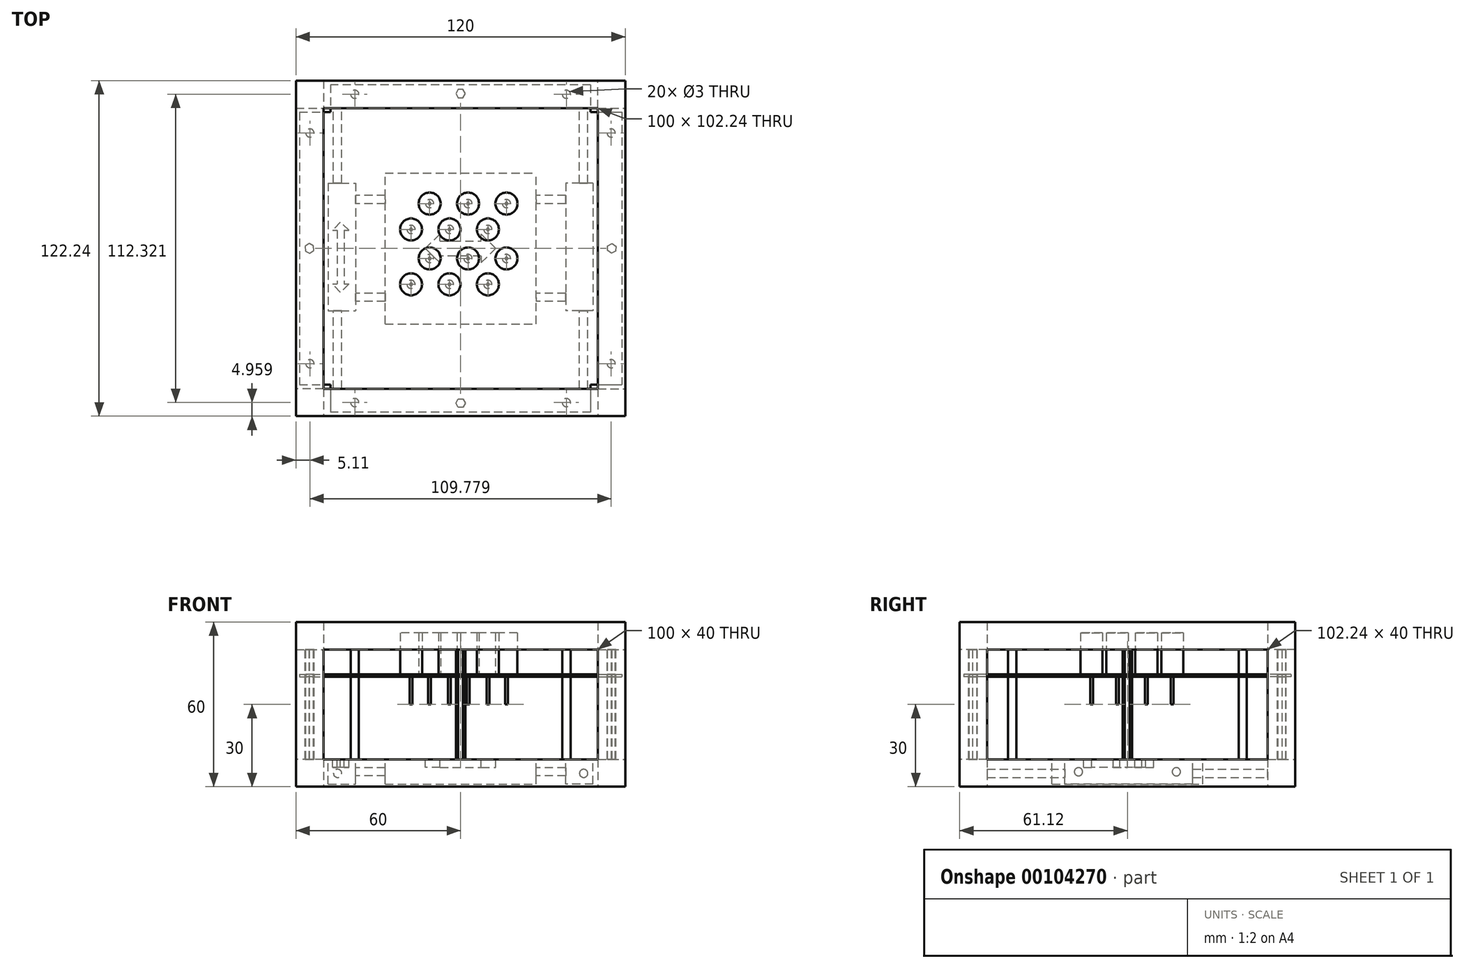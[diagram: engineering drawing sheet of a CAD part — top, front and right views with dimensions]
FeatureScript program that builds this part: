
annotation { "Feature Type Name" : "Feature", "Feature Type Description" : "" }
export const myFeature = defineFeature(function(context is Context, id is Id, definition is map)
    precondition{}
    {
        {
            var Q0;
            Q0=qCreatedBy(makeId("Top.planeOp"),FACE);
            var sketch = newSketch(context, id + "F0", { "sketchPlane" : qUnion([Q0])});
            skLineSegment(sketch, "E0.bottom", {"start": v(60, 61.12) * mm, "end": v(-60, 61.12) * mm});
            skLineSegment(sketch, "E0.top", {"start": v(60, -61.12) * mm, "end": v(-60, -61.12) * mm});
            skLineSegment(sketch, "E0.left", {"start": v(60, 61.12) * mm, "end": v(60, -61.12) * mm});
            skLineSegment(sketch, "E0.right", {"start": v(-60, 61.12) * mm, "end": v(-60, -61.12) * mm});
            skPoint(sketch, "E0.middle", {"position": v(0, 0) * mm});
            skLineSegment(sketch, "E1.bottom", {"start": v(50, 51.12) * mm, "end": v(-50, 51.12) * mm});
            skLineSegment(sketch, "E1.top", {"start": v(50, -51.12) * mm, "end": v(-50, -51.12) * mm});
            skLineSegment(sketch, "E1.left", {"start": v(50, 51.12) * mm, "end": v(50, -51.12) * mm});
            skLineSegment(sketch, "E1.right", {"start": v(-50, 51.12) * mm, "end": v(-50, -51.12) * mm});
            skSolve(sketch);
        }
        {
            var Q0;
            Q0 = qSketchRegion(id + "F0", true);
            extrude(context, id + "F1", {"entities" : qUnion([Q0]), "depth" : 10 * mm});
        }
        {
            var Q0;
            Q0=makeQuery(id+"F1.opExtrude","CAP_FACE",FACE,{"disambiguationData":[OSD([sQuery(id+"F0.wireOp",EDGE,"E0.bottom"),sQuery(id+"F0.wireOp",EDGE,"E0.top"),sQuery(id+"F0.wireOp",EDGE,"E0.left"),sQuery(id+"F0.wireOp",EDGE,"E0.right"),sQuery(id+"F0.wireOp",EDGE,"E1.bottom"),sQuery(id+"F0.wireOp",EDGE,"E1.top"),sQuery(id+"F0.wireOp",EDGE,"E1.left"),sQuery(id+"F0.wireOp",EDGE,"E1.right")])],"isStart":false});
            var sketch = newSketch(context, id + "F2", { "sketchPlane" : qUnion([Q0])});
            skLineSegment(sketch, "E2.bottom", {"start": v(-60, 61.12) * mm, "end": v(-50, 61.12) * mm});
            skLineSegment(sketch, "E2.top", {"start": v(-60, 51.12) * mm, "end": v(-50, 51.12) * mm});
            skLineSegment(sketch, "E2.left", {"start": v(-60, 61.12) * mm, "end": v(-60, 51.12) * mm});
            skLineSegment(sketch, "E2.right", {"start": v(-50, 61.12) * mm, "end": v(-50, 51.12) * mm});
            skLineSegment(sketch, "E3.bottom", {"start": v(50, 51.12) * mm, "end": v(60, 51.12) * mm});
            skLineSegment(sketch, "E3.top", {"start": v(50, 61.12) * mm, "end": v(60, 61.12) * mm});
            skLineSegment(sketch, "E3.left", {"start": v(50, 51.12) * mm, "end": v(50, 61.12) * mm});
            skLineSegment(sketch, "E3.right", {"start": v(60, 51.12) * mm, "end": v(60, 61.12) * mm});
            skLineSegment(sketch, "E4.bottom", {"start": v(50, -51.12) * mm, "end": v(60, -51.12) * mm});
            skLineSegment(sketch, "E4.top", {"start": v(50, -61.12) * mm, "end": v(60, -61.12) * mm});
            skLineSegment(sketch, "E4.left", {"start": v(50, -51.12) * mm, "end": v(50, -61.12) * mm});
            skLineSegment(sketch, "E4.right", {"start": v(60, -51.12) * mm, "end": v(60, -61.12) * mm});
            skLineSegment(sketch, "E5.bottom", {"start": v(-50, -51.12) * mm, "end": v(-60, -51.12) * mm});
            skLineSegment(sketch, "E5.top", {"start": v(-50, -61.12) * mm, "end": v(-60, -61.12) * mm});
            skLineSegment(sketch, "E5.left", {"start": v(-50, -51.12) * mm, "end": v(-50, -61.12) * mm});
            skLineSegment(sketch, "E5.right", {"start": v(-60, -51.12) * mm, "end": v(-60, -61.12) * mm});
            skSolve(sketch);
        }
        {
            var Q0;
            Q0 = qSketchRegion(id + "F2", true);
            extrude(context, id + "F3", {"entities" : qUnion([Q0]), "operationType" : NewBodyOperationType.ADD, "depth" : 40 * mm});
        }
        {
            var Q0;
            Q0=makeQuery(id+"F3.opExtrude","CAP_FACE",FACE,{"disambiguationData":[OSD([sQuery(id+"F2.wireOp",EDGE,"E2.bottom"),sQuery(id+"F2.wireOp",EDGE,"E2.top"),sQuery(id+"F2.wireOp",EDGE,"E2.left"),sQuery(id+"F2.wireOp",EDGE,"E2.right")])],"isStart":false});
            var sketch = newSketch(context, id + "F4", { "sketchPlane" : qUnion([Q0])});
            skPoint(sketch, "E6.0", {"position": v(-50, 51.12) * mm});
            skPoint(sketch, "E7.0", {"position": v(-60, 61.12) * mm});
            skPoint(sketch, "E8.0", {"position": v(50, -51.12) * mm});
            skPoint(sketch, "E9.0", {"position": v(60, -61.12) * mm});
            skLineSegment(sketch, "E10.bottom", {"start": v(-60, 61.12) * mm, "end": v(60, 61.12) * mm});
            skLineSegment(sketch, "E10.top", {"start": v(-60, -61.12) * mm, "end": v(60, -61.12) * mm});
            skLineSegment(sketch, "E10.left", {"start": v(-60, 61.12) * mm, "end": v(-60, -61.12) * mm});
            skLineSegment(sketch, "E10.right", {"start": v(60, 61.12) * mm, "end": v(60, -61.12) * mm});
            skLineSegment(sketch, "E11.bottom", {"start": v(-50, 51.12) * mm, "end": v(50, 51.12) * mm});
            skLineSegment(sketch, "E11.top", {"start": v(-50, -51.12) * mm, "end": v(50, -51.12) * mm});
            skLineSegment(sketch, "E11.left", {"start": v(-50, 51.12) * mm, "end": v(-50, -51.12) * mm});
            skLineSegment(sketch, "E11.right", {"start": v(50, 51.12) * mm, "end": v(50, -51.12) * mm});
            skSolve(sketch);
        }
        {
            var Q0;
            Q0 = qSketchRegion(id + "F4", true);
            extrude(context, id + "F5", {"entities" : qUnion([Q0]), "operationType" : NewBodyOperationType.ADD, "depth" : 10 * mm});
        }
        {
            var Q0;
            Q0=makeQuery(id+"F1.opExtrude","SWEPT_FACE",FACE,{"disambiguationData":[OSD([sQuery(id+"F0.wireOp",EDGE,"E1.bottom")])]});
            var sketch = newSketch(context, id + "F6", { "sketchPlane" : qUnion([Q0])});
            skLineSegment(sketch, "E12", {"start": v(0, 0) * mm, "end": v(0, 109.63) * mm, "construction": true});
            skCircle(sketch, "E13", {"center": v(-44.83, 4.86) * mm, "radius": 1.5 * mm});
            skCircle(sketch, "E14.MirrorC", {"center": v(44.83, 4.86) * mm, "radius": 1.5 * mm});
            skSolve(sketch);
        }
        {
            var Q0;
            Q0 = qSketchRegion(id + "F6", true);
            extrude(context, id + "F7", {"entities" : qUnion([Q0]), "operationType" : NewBodyOperationType.ADD, "endBound" : BoundingType.UP_TO_NEXT, "depth" : 25 * mm});
        }
        {
            var Q0;
            Q0=makeQuery(id+"F5.opExtrude","CAP_FACE",FACE,{"disambiguationData":[OSD([sQuery(id+"F4.wireOp",EDGE,"E10.bottom"),sQuery(id+"F4.wireOp",EDGE,"E10.top"),sQuery(id+"F4.wireOp",EDGE,"E10.left"),sQuery(id+"F4.wireOp",EDGE,"E10.right"),sQuery(id+"F4.wireOp",EDGE,"E11.bottom"),sQuery(id+"F4.wireOp",EDGE,"E11.top"),sQuery(id+"F4.wireOp",EDGE,"E11.left"),sQuery(id+"F4.wireOp",EDGE,"E11.right")])],"isStart":false});
            var sketch = newSketch(context, id + "F8", { "sketchPlane" : qUnion([Q0])});
            skCircle(sketch, "E15", {"center": v(-38.56, 56.16) * mm, "radius": 1.5 * mm});
            skCircle(sketch, "E16", {"center": v(-54.89, 42.03) * mm, "radius": 1.5 * mm});
            skCircle(sketch, "E17.MirrorC", {"center": v(38.56, 56.16) * mm, "radius": 1.5 * mm});
            skCircle(sketch, "E18.MirrorC", {"center": v(-54.89, -42.03) * mm, "radius": 1.5 * mm});
            skCircle(sketch, "E19.MirrorC", {"center": v(54.89, 42.03) * mm, "radius": 1.5 * mm});
            skCircle(sketch, "E20.MirrorC", {"center": v(54.89, -42.03) * mm, "radius": 1.5 * mm});
            skCircle(sketch, "E21.MirrorC", {"center": v(-38.56, -56.16) * mm, "radius": 1.5 * mm});
            skCircle(sketch, "E22.MirrorC", {"center": v(38.56, -56.16) * mm, "radius": 1.5 * mm});
            skCircle(sketch, "E23.cCircle", {"center": v(0, 56.37) * mm, "radius": 1.5 * mm, "construction": true});
            skLineSegment(sketch, "E23.0", {"start": v(0.87, 54.87) * mm, "end": v(-0.87, 54.87) * mm});
            skLineSegment(sketch, "E23.1", {"start": v(-0.87, 54.87) * mm, "end": v(-1.73, 56.37) * mm});
            skLineSegment(sketch, "E23.2", {"start": v(-1.73, 56.37) * mm, "end": v(-0.87, 57.87) * mm});
            skLineSegment(sketch, "E23.3", {"start": v(-0.87, 57.87) * mm, "end": v(0.87, 57.87) * mm});
            skLineSegment(sketch, "E23.4", {"start": v(0.87, 57.87) * mm, "end": v(1.73, 56.37) * mm});
            skLineSegment(sketch, "E23.5", {"start": v(1.73, 56.37) * mm, "end": v(0.87, 54.87) * mm});
            skPoint(sketch, "E23.0.midPoint", {"position": v(0, 54.87) * mm});
            skCircle(sketch, "E24.cCircle", {"center": v(-55.08, 0) * mm, "radius": 1.5 * mm, "construction": true});
            skLineSegment(sketch, "E24.0", {"start": v(-55.17, 1.73) * mm, "end": v(-53.62, 0.94) * mm});
            skLineSegment(sketch, "E24.1", {"start": v(-53.62, 0.94) * mm, "end": v(-53.54, -0.79) * mm});
            skLineSegment(sketch, "E24.2", {"start": v(-53.54, -0.79) * mm, "end": v(-55, -1.73) * mm});
            skLineSegment(sketch, "E24.3", {"start": v(-55, -1.73) * mm, "end": v(-56.54, -0.94) * mm});
            skLineSegment(sketch, "E24.4", {"start": v(-56.54, -0.94) * mm, "end": v(-56.62, 0.79) * mm});
            skLineSegment(sketch, "E24.5", {"start": v(-56.62, 0.79) * mm, "end": v(-55.17, 1.73) * mm});
            skPoint(sketch, "E24.0.midPoint", {"position": v(-54.4, 1.34) * mm});
            skCircle(sketch, "E25.MirrorC", {"center": v(0, -56.37) * mm, "radius": 1.5 * mm, "construction": true});
            skLineSegment(sketch, "E26.MirrorCS", {"start": v(-0.87, -57.87) * mm, "end": v(0.87, -57.87) * mm});
            skLineSegment(sketch, "E27.MirrorCS", {"start": v(-1.73, -56.37) * mm, "end": v(-0.87, -57.87) * mm});
            skLineSegment(sketch, "E28.MirrorCS", {"start": v(0.87, -57.87) * mm, "end": v(1.73, -56.37) * mm});
            skLineSegment(sketch, "E29.MirrorCS", {"start": v(1.73, -56.37) * mm, "end": v(0.87, -54.87) * mm});
            skLineSegment(sketch, "E30.MirrorCS", {"start": v(-0.87, -54.87) * mm, "end": v(-1.73, -56.37) * mm});
            skLineSegment(sketch, "E31.MirrorCS", {"start": v(0.87, -54.87) * mm, "end": v(-0.87, -54.87) * mm});
            skPoint(sketch, "E32.MirrorP", {"position": v(0, -54.87) * mm});
            skLineSegment(sketch, "E33.MirrorCS", {"start": v(56.62, 0.79) * mm, "end": v(55.17, 1.73) * mm});
            skLineSegment(sketch, "E34.MirrorCS", {"start": v(53.62, 0.94) * mm, "end": v(53.54, -0.79) * mm});
            skLineSegment(sketch, "E35.MirrorCS", {"start": v(56.54, -0.94) * mm, "end": v(56.62, 0.79) * mm});
            skCircle(sketch, "E36.MirrorC", {"center": v(55.08, 0) * mm, "radius": 1.5 * mm, "construction": true});
            skLineSegment(sketch, "E37.MirrorCS", {"start": v(55.17, 1.73) * mm, "end": v(53.62, 0.94) * mm});
            skLineSegment(sketch, "E38.MirrorCS", {"start": v(53.54, -0.79) * mm, "end": v(55, -1.73) * mm});
            skLineSegment(sketch, "E39.MirrorCS", {"start": v(55, -1.73) * mm, "end": v(56.54, -0.94) * mm});
            skPoint(sketch, "E40.MirrorP", {"position": v(54.4, 1.34) * mm});
            skSolve(sketch);
        }
        {
            var Q0;
            Q0 = qSketchRegion(id + "F8", true);
            var Q1;
            {var subQ0=sQuery(id+"F0.wireOp",EDGE,"E0.bottom");var subQ1=sQuery(id+"F0.wireOp",EDGE,"E1.right");var subQ2=sQuery(id+"F0.wireOp",EDGE,"E1.left");var subQ3=sQuery(id+"F0.wireOp",EDGE,"E1.bottom");var subQ4=makeQuery(id+"F1.opExtrude","CAP_FACE",FACE,{"disambiguationData":[OSD([subQ0,sQuery(id+"F0.wireOp",EDGE,"E0.top"),sQuery(id+"F0.wireOp",EDGE,"E0.left"),sQuery(id+"F0.wireOp",EDGE,"E0.right"),subQ3,sQuery(id+"F0.wireOp",EDGE,"E1.top"),subQ2,subQ1])],"isStart":false});Q1=makeQuery(id+"F3.boolean.opBoolean","SPLIT",FACE,{"disambiguationData":[TD([makeQuery(id+"F1.opExtrude","SWEPT_FACE",FACE,{"disambiguationData":[OSD([subQ0])]})])],"derivedFrom":subQ4});}
            extrude(context, id + "F9", {"entities" : qUnion([Q0]), "operationType" : NewBodyOperationType.ADD, "endBound" : BoundingType.UP_TO_SURFACE, "oppositeDirection" : true, "endBoundEntityFace" : qUnion([Q1]), "depth" : 25 * mm});
        }
        {
            var Q0;
            Q0=qCreatedBy(makeId("Top.planeOp"),FACE);
            cPlane(context, id + "F10", {"entities" : qUnion([Q0]), "cplaneType" : CPlaneType.OFFSET, "offset" : 40 * mm, "width" : 150 * mm, "height" : 150 * mm});
        }
        {
            var Q0;
            Q0=qCreatedBy(id+"F10.planeOp",FACE);
            var sketch = newSketch(context, id + "F11", { "sketchPlane" : qUnion([Q0])});
            skLineSegment(sketch, "E41.bottom", {"start": v(47.38, 59.63) * mm, "end": v(-47.38, 59.63) * mm});
            skLineSegment(sketch, "E41.top", {"start": v(47.38, -59.63) * mm, "end": v(-47.38, -59.63) * mm});
            skLineSegment(sketch, "E41.left", {"start": v(47.38, 59.63) * mm, "end": v(47.38, 49.62) * mm});
            skLineSegment(sketch, "E41.right", {"start": v(-47.38, 59.63) * mm, "end": v(-47.38, 49.62) * mm});
            skLineSegment(sketch, "E42.bottom", {"start": v(-58.75, 49.62) * mm, "end": v(-47.38, 49.62) * mm});
            skLineSegment(sketch, "E42.top", {"start": v(-58.75, -49.62) * mm, "end": v(-47.38, -49.62) * mm});
            skLineSegment(sketch, "E42.left", {"start": v(-58.75, 49.62) * mm, "end": v(-58.75, -49.62) * mm});
            skLineSegment(sketch, "E42.right", {"start": v(58.75, 49.62) * mm, "end": v(58.75, -49.62) * mm});
            skLineSegment(sketch, "E43.trimOffspring", {"start": v(47.38, 49.62) * mm, "end": v(58.75, 49.62) * mm});
            skLineSegment(sketch, "E44.trimOffspring", {"start": v(47.38, -49.62) * mm, "end": v(47.38, -59.63) * mm});
            skLineSegment(sketch, "E45.trimOffspring", {"start": v(-47.38, -49.62) * mm, "end": v(-47.38, -59.63) * mm});
            skLineSegment(sketch, "E46.trimOffspring", {"start": v(47.38, -49.62) * mm, "end": v(58.75, -49.62) * mm});
            skCircle(sketch, "E47.0", {"center": v(-38.56, 56.16) * mm, "radius": 1.5 * mm});
            skCircle(sketch, "E48.0", {"center": v(38.56, 56.16) * mm, "radius": 1.5 * mm});
            skCircle(sketch, "E49.0", {"center": v(-54.89, 42.03) * mm, "radius": 1.5 * mm});
            skCircle(sketch, "E50.0", {"center": v(-54.89, -42.03) * mm, "radius": 1.5 * mm});
            skCircle(sketch, "E51.0", {"center": v(54.89, -42.03) * mm, "radius": 1.5 * mm});
            skCircle(sketch, "E52.0", {"center": v(54.89, 42.03) * mm, "radius": 1.5 * mm});
            skCircle(sketch, "E53.0", {"center": v(38.56, -56.16) * mm, "radius": 1.5 * mm});
            skCircle(sketch, "E54.0", {"center": v(-38.56, -56.16) * mm, "radius": 1.5 * mm});
            skLineSegment(sketch, "E55.direction1", {"start": v(1.86, 29.02) * mm, "end": v(26.86, 29.02) * mm, "construction": true});
            skPoint(sketch, "E56.middle", {"position": v(0.85, -12.7) * mm});
            skCircle(sketch, "E57", {"center": v(-11.29, 16.33) * mm, "radius": 1.5 * mm});
            skCircle(sketch, "E58", {"center": v(2.71, 16.33) * mm, "radius": 1.5 * mm});
            skCircle(sketch, "E59", {"center": v(16.71, 16.33) * mm, "radius": 1.5 * mm});
            skCircle(sketch, "E60", {"center": v(-18.06, 6.9) * mm, "radius": 1.5 * mm});
            skCircle(sketch, "E61", {"center": v(-4.06, 6.9) * mm, "radius": 1.5 * mm});
            skCircle(sketch, "E62", {"center": v(9.94, 6.9) * mm, "radius": 1.5 * mm});
            skCircle(sketch, "E63.0.1.0", {"center": v(2.71, -3.67) * mm, "radius": 1.5 * mm});
            skCircle(sketch, "E63.0.1.1", {"center": v(16.71, -3.67) * mm, "radius": 1.5 * mm});
            skCircle(sketch, "E63.0.1.2", {"center": v(-18.06, -13.1) * mm, "radius": 1.5 * mm});
            skCircle(sketch, "E63.0.1.3", {"center": v(-4.06, -13.1) * mm, "radius": 1.5 * mm});
            skCircle(sketch, "E63.0.1.4", {"center": v(9.94, -13.1) * mm, "radius": 1.5 * mm});
            skCircle(sketch, "E63.0.1.5", {"center": v(-11.29, -3.67) * mm, "radius": 1.5 * mm});
            skLineSegment(sketch, "E63.direction2", {"start": v(2.71, 16.33) * mm, "end": v(2.71, -3.67) * mm, "construction": true});
            skSolve(sketch);
        }
        {
            var Q0;
            Q0 = qSketchRegion(id + "F11", true);
            extrude(context, id + "F12", {"entities" : qUnion([Q0]), "depth" : 1 * mm});
        }
        {
            var Q0;
            Q0=makeQuery(id+"F12.opExtrude","CAP_FACE",FACE,{"disambiguationData":[OSD([sQuery(id+"F11.wireOp",EDGE,"E41.bottom"),sQuery(id+"F11.wireOp",EDGE,"E41.top"),sQuery(id+"F11.wireOp",EDGE,"E41.left"),sQuery(id+"F11.wireOp",EDGE,"E41.right"),sQuery(id+"F11.wireOp",EDGE,"E42.bottom"),sQuery(id+"F11.wireOp",EDGE,"E42.top"),sQuery(id+"F11.wireOp",EDGE,"E42.left"),sQuery(id+"F11.wireOp",EDGE,"E42.right"),sQuery(id+"F11.wireOp",EDGE,"E43.trimOffspring"),sQuery(id+"F11.wireOp",EDGE,"E44.trimOffspring"),sQuery(id+"F11.wireOp",EDGE,"E45.trimOffspring"),sQuery(id+"F11.wireOp",EDGE,"E46.trimOffspring"),sQuery(id+"F11.wireOp",EDGE,"E47.0"),sQuery(id+"F11.wireOp",EDGE,"E48.0"),sQuery(id+"F11.wireOp",EDGE,"E49.0"),sQuery(id+"F11.wireOp",EDGE,"E50.0"),sQuery(id+"F11.wireOp",EDGE,"E51.0"),sQuery(id+"F11.wireOp",EDGE,"E52.0"),sQuery(id+"F11.wireOp",EDGE,"E53.0"),sQuery(id+"F11.wireOp",EDGE,"E54.0"),sQuery(id+"F11.wireOp",EDGE,"N9pgbSyz-TjTt-8bTq-EJYd-xtjQmETEgeIH"),sQuery(id+"F11.wireOp",EDGE,"ememrni6-0ryD-3c4K-8yvm-Dv3rnywVcJe6"),sQuery(id+"F11.wireOp",EDGE,"GpeT1Jka-8UNp-yT1Z-DerH-8jlBy2sCrnBp"),sQuery(id+"F11.wireOp",EDGE,"57d6f0b1-a59f-44bf-8e70-e7ba8592d35d"),sQuery(id+"F11.wireOp",EDGE,"85515dfb-5310-43cc-a585-7a81776eaa21"),sQuery(id+"F11.wireOp",EDGE,"b182f581-29e2-42ea-8fef-9c266fc4cbda"),sQuery(id+"F11.wireOp",EDGE,"E55.0.1.0"),sQuery(id+"F11.wireOp",EDGE,"E55.0.1.1"),sQuery(id+"F11.wireOp",EDGE,"E55.0.1.2"),sQuery(id+"F11.wireOp",EDGE,"E55.0.1.3"),sQuery(id+"F11.wireOp",EDGE,"E55.0.1.4"),sQuery(id+"F11.wireOp",EDGE,"E55.0.1.5"),sQuery(id+"F11.wireOp",EDGE,"E55.0.2.0"),sQuery(id+"F11.wireOp",EDGE,"E55.0.2.1"),sQuery(id+"F11.wireOp",EDGE,"E55.0.2.2"),sQuery(id+"F11.wireOp",EDGE,"E55.0.2.3"),sQuery(id+"F11.wireOp",EDGE,"E55.0.2.4"),sQuery(id+"F11.wireOp",EDGE,"E55.0.2.5")])],"isStart":false});
            var sketch = newSketch(context, id + "F13", { "sketchPlane" : qUnion([Q0])});
            skCircle(sketch, "E64", {"center": v(-11.29, 16.33) * mm, "radius": 4 * mm});
            skCircle(sketch, "E65", {"center": v(2.71, 16.33) * mm, "radius": 4 * mm});
            skCircle(sketch, "E66", {"center": v(16.71, 16.33) * mm, "radius": 4 * mm});
            skCircle(sketch, "E67", {"center": v(-18.06, 6.9) * mm, "radius": 4 * mm});
            skCircle(sketch, "E68", {"center": v(-4.06, 6.9) * mm, "radius": 4 * mm});
            skCircle(sketch, "E69", {"center": v(9.94, 6.9) * mm, "radius": 4 * mm});
            skCircle(sketch, "E70", {"center": v(-11.29, -3.67) * mm, "radius": 4 * mm});
            skCircle(sketch, "E71", {"center": v(-18.06, -13.1) * mm, "radius": 4 * mm});
            skCircle(sketch, "E72", {"center": v(2.71, -3.67) * mm, "radius": 4 * mm});
            skCircle(sketch, "E73", {"center": v(16.71, -3.67) * mm, "radius": 4 * mm});
            skCircle(sketch, "E74", {"center": v(-4.06, -13.1) * mm, "radius": 4 * mm});
            skCircle(sketch, "E75", {"center": v(9.94, -13.1) * mm, "radius": 4 * mm});
            skSolve(sketch);
        }
        {
            var Q0;
            Q0 = qSketchRegion(id + "F13", true);
            extrude(context, id + "F14", {"entities" : qUnion([Q0]), "depth" : 15 * mm});
        }
        {
            var Q0;
            Q0=makeQuery(id+"F12.opExtrude","CAP_FACE",FACE,{"disambiguationData":[OSD([sQuery(id+"F11.wireOp",EDGE,"E41.bottom"),sQuery(id+"F11.wireOp",EDGE,"E41.top"),sQuery(id+"F11.wireOp",EDGE,"E41.left"),sQuery(id+"F11.wireOp",EDGE,"E41.right"),sQuery(id+"F11.wireOp",EDGE,"E42.bottom"),sQuery(id+"F11.wireOp",EDGE,"E42.top"),sQuery(id+"F11.wireOp",EDGE,"E42.left"),sQuery(id+"F11.wireOp",EDGE,"E42.right"),sQuery(id+"F11.wireOp",EDGE,"E43.trimOffspring"),sQuery(id+"F11.wireOp",EDGE,"E44.trimOffspring"),sQuery(id+"F11.wireOp",EDGE,"E45.trimOffspring"),sQuery(id+"F11.wireOp",EDGE,"E46.trimOffspring"),sQuery(id+"F11.wireOp",EDGE,"E47.0"),sQuery(id+"F11.wireOp",EDGE,"E48.0"),sQuery(id+"F11.wireOp",EDGE,"E49.0"),sQuery(id+"F11.wireOp",EDGE,"E50.0"),sQuery(id+"F11.wireOp",EDGE,"E51.0"),sQuery(id+"F11.wireOp",EDGE,"E52.0"),sQuery(id+"F11.wireOp",EDGE,"E53.0"),sQuery(id+"F11.wireOp",EDGE,"E54.0"),sQuery(id+"F11.wireOp",EDGE,"E57"),sQuery(id+"F11.wireOp",EDGE,"E58"),sQuery(id+"F11.wireOp",EDGE,"E59"),sQuery(id+"F11.wireOp",EDGE,"E60"),sQuery(id+"F11.wireOp",EDGE,"E61"),sQuery(id+"F11.wireOp",EDGE,"E62"),sQuery(id+"F11.wireOp",EDGE,"E63.0.1.0"),sQuery(id+"F11.wireOp",EDGE,"E63.0.1.1"),sQuery(id+"F11.wireOp",EDGE,"E63.0.1.2"),sQuery(id+"F11.wireOp",EDGE,"E63.0.1.3"),sQuery(id+"F11.wireOp",EDGE,"E63.0.1.4"),sQuery(id+"F11.wireOp",EDGE,"E63.0.1.5")])],"isStart":true});
            var sketch = newSketch(context, id + "F15", { "sketchPlane" : qUnion([Q0])});
            skCircle(sketch, "E76", {"center": v(-18.06, 13.1) * mm, "radius": 0.5 * mm});
            skCircle(sketch, "E77", {"center": v(-4.06, 13.1) * mm, "radius": 0.5 * mm});
            skCircle(sketch, "E78", {"center": v(9.94, 13.1) * mm, "radius": 0.5 * mm});
            skCircle(sketch, "E79", {"center": v(-11.29, 3.67) * mm, "radius": 0.5 * mm});
            skCircle(sketch, "E80", {"center": v(2.71, 3.67) * mm, "radius": 0.5 * mm});
            skCircle(sketch, "E81", {"center": v(16.71, 3.67) * mm, "radius": 0.5 * mm});
            skCircle(sketch, "E82", {"center": v(-18.06, -6.9) * mm, "radius": 0.5 * mm});
            skCircle(sketch, "E83", {"center": v(-4.06, -6.9) * mm, "radius": 0.5 * mm});
            skCircle(sketch, "E84", {"center": v(9.94, -6.9) * mm, "radius": 0.5 * mm});
            skCircle(sketch, "E85", {"center": v(-11.29, -16.33) * mm, "radius": 0.5 * mm});
            skCircle(sketch, "E86", {"center": v(2.71, -16.33) * mm, "radius": 0.5 * mm});
            skCircle(sketch, "E87", {"center": v(16.71, -16.33) * mm, "radius": 0.5 * mm});
            skSolve(sketch);
        }
        {
            var Q0;
            Q0 = qSketchRegion(id + "F15", true);
            extrude(context, id + "F16", {"entities" : qUnion([Q0]), "depth" : 10 * mm});
        }
        {
            var Q0;
            {var subQ0=sQuery(id+"F0.wireOp",EDGE,"E1.top");var subQ1=sQuery(id+"F0.wireOp",EDGE,"E1.right");var subQ2=sQuery(id+"F0.wireOp",EDGE,"E1.bottom");var subQ3=sQuery(id+"F0.wireOp",EDGE,"E0.right");var subQ4=makeQuery(id+"F1.opExtrude","CAP_FACE",FACE,{"disambiguationData":[OSD([sQuery(id+"F0.wireOp",EDGE,"E0.bottom"),sQuery(id+"F0.wireOp",EDGE,"E0.top"),sQuery(id+"F0.wireOp",EDGE,"E0.left"),subQ3,subQ2,subQ0,sQuery(id+"F0.wireOp",EDGE,"E1.left"),subQ1])],"isStart":false});Q0=makeQuery(id+"F3.boolean.opBoolean","SPLIT",FACE,{"disambiguationData":[TD([makeQuery(id+"F1.opExtrude","SWEPT_FACE",FACE,{"disambiguationData":[OSD([subQ3])]})])],"derivedFrom":subQ4});}
            var sketch = newSketch(context, id + "F17", { "sketchPlane" : qUnion([Q0])});
            skLineSegment(sketch, "E88.bottom", {"start": v(-48.27, 23.8) * mm, "end": v(-38.27, 23.8) * mm});
            skLineSegment(sketch, "E88.top", {"start": v(-48.27, -22.75) * mm, "end": v(-38.27, -22.75) * mm});
            skLineSegment(sketch, "E88.left", {"start": v(-48.27, 23.8) * mm, "end": v(-48.27, -22.75) * mm});
            skLineSegment(sketch, "E88.right", {"start": v(-38.27, 23.8) * mm, "end": v(-38.27, -22.75) * mm});
            skLineSegment(sketch, "E89.MirrorCS", {"start": v(38.27, 23.8) * mm, "end": v(38.27, -22.75) * mm});
            skLineSegment(sketch, "E90.MirrorCS", {"start": v(48.27, 23.8) * mm, "end": v(48.27, -22.75) * mm});
            skLineSegment(sketch, "E91.MirrorCS", {"start": v(48.27, 23.8) * mm, "end": v(38.27, 23.8) * mm});
            skLineSegment(sketch, "E92.MirrorCS", {"start": v(48.27, -22.75) * mm, "end": v(38.27, -22.75) * mm});
            skSolve(sketch);
        }
        {
            var Q0;
            Q0 = qSketchRegion(id + "F17", true);
            extrude(context, id + "F18", {"entities" : qUnion([Q0]), "operationType" : NewBodyOperationType.ADD, "oppositeDirection" : true, "depth" : 9 * mm});
        }
        {
            var Q0;
            Q0=makeQuery(id+"F18.opExtrude","SWEPT_FACE",FACE,{"disambiguationData":[OSD([sQuery(id+"F17.wireOp",EDGE,"E88.right")])]});
            var sketch = newSketch(context, id + "F19", { "sketchPlane" : qUnion([Q0])});
            skCircle(sketch, "E93", {"center": v(-17.83, 5.44) * mm, "radius": 1.5 * mm});
            skCircle(sketch, "E94.MirrorC", {"center": v(17.83, 5.44) * mm, "radius": 1.5 * mm});
            skSolve(sketch);
        }
        {
            var Q0;
            Q0 = qSketchRegion(id + "F19", true);
            extrude(context, id + "F20", {"entities" : qUnion([Q0]), "operationType" : NewBodyOperationType.ADD, "endBound" : BoundingType.UP_TO_NEXT, "depth" : 25 * mm});
        }
        {
            var Q0;
            Q0=makeQuery(id+"F18.opExtrude","CAP_FACE",FACE,{"disambiguationData":[OSD([sQuery(id+"F17.wireOp",EDGE,"E88.bottom"),sQuery(id+"F17.wireOp",EDGE,"E88.top"),sQuery(id+"F17.wireOp",EDGE,"E88.left"),sQuery(id+"F17.wireOp",EDGE,"E88.right")])],"isStart":true});
            var sketch = newSketch(context, id + "F21", { "sketchPlane" : qUnion([Q0])});
            skLineSegment(sketch, "E95.bottom", {"start": v(-27.5, -27.5) * mm, "end": v(27.5, -27.5) * mm});
            skLineSegment(sketch, "E95.top", {"start": v(-27.5, 27.5) * mm, "end": v(27.5, 27.5) * mm});
            skLineSegment(sketch, "E95.left", {"start": v(-27.5, -27.5) * mm, "end": v(-27.5, 27.5) * mm});
            skLineSegment(sketch, "E95.right", {"start": v(27.5, -27.5) * mm, "end": v(27.5, 27.5) * mm});
            skPoint(sketch, "E95.middle", {"position": v(0, 0) * mm});
            skSolve(sketch);
        }
        {
            var Q0;
            Q0 = qSketchRegion(id + "F21", true);
            extrude(context, id + "F22", {"entities" : qUnion([Q0]), "operationType" : NewBodyOperationType.ADD, "oppositeDirection" : true, "depth" : 9 * mm});
        }
        {
            var Q0;
            Q0=makeQuery(id+"F22.opExtrude","CAP_FACE",FACE,{"disambiguationData":[OSD([sQuery(id+"F21.wireOp",EDGE,"E95.bottom"),sQuery(id+"F21.wireOp",EDGE,"E95.top"),sQuery(id+"F21.wireOp",EDGE,"E95.left"),sQuery(id+"F21.wireOp",EDGE,"E95.right")])],"isStart":true});
            var sketch = newSketch(context, id + "F23", { "sketchPlane" : qUnion([Q0])});
            skLineSegment(sketch, "E96", {"start": v(0, -2.72) * mm, "end": v(7.5, -2.72) * mm});
            skLineSegment(sketch, "E97", {"start": v(7.5, -2.72) * mm, "end": v(7.5, -5.2) * mm});
            skLineSegment(sketch, "E98", {"start": v(7.5, -5.2) * mm, "end": v(12.83, 0) * mm});
            skLineSegment(sketch, "E99.MirrorCS", {"start": v(7.5, 2.72) * mm, "end": v(7.5, 5.2) * mm});
            skLineSegment(sketch, "E100.MirrorCS", {"start": v(0, 2.72) * mm, "end": v(7.5, 2.72) * mm});
            skLineSegment(sketch, "E101.MirrorCS", {"start": v(7.5, 5.2) * mm, "end": v(12.83, 0) * mm});
            skLineSegment(sketch, "E102.MirrorCS", {"start": v(-7.5, -2.72) * mm, "end": v(-7.5, -5.2) * mm});
            skLineSegment(sketch, "E103.MirrorCS", {"start": v(-7.5, 2.72) * mm, "end": v(-7.5, 5.2) * mm});
            skLineSegment(sketch, "E104.MirrorCS", {"start": v(-7.5, 5.2) * mm, "end": v(-12.83, 0) * mm});
            skLineSegment(sketch, "E105.MirrorCS", {"start": v(0, 2.72) * mm, "end": v(-7.5, 2.72) * mm});
            skLineSegment(sketch, "E106.MirrorCS", {"start": v(-7.5, -5.2) * mm, "end": v(-12.83, 0) * mm});
            skLineSegment(sketch, "E107.MirrorCS", {"start": v(0, -2.72) * mm, "end": v(-7.5, -2.72) * mm});
            skSolve(sketch);
        }
        {
            var Q0;
            Q0 = qSketchRegion(id + "F23", true);
            extrude(context, id + "F24", {"entities" : qUnion([Q0]), "operationType" : NewBodyOperationType.REMOVE, "oppositeDirection" : true, "depth" : 3 * mm});
        }
        {
            var Q0;
            Q0=makeQuery(id+"F18.opExtrude","CAP_FACE",FACE,{"disambiguationData":[OSD([sQuery(id+"F17.wireOp",EDGE,"E88.bottom"),sQuery(id+"F17.wireOp",EDGE,"E88.top"),sQuery(id+"F17.wireOp",EDGE,"E88.left"),sQuery(id+"F17.wireOp",EDGE,"E88.right")])],"isStart":true});
            var sketch = newSketch(context, id + "F25", { "sketchPlane" : qUnion([Q0])});
            skLineSegment(sketch, "E108", {"start": v(-42.48, -3.2) * mm, "end": v(-42.48, -13) * mm});
            skLineSegment(sketch, "E109", {"start": v(-42.48, -13) * mm, "end": v(-40.71, -13) * mm});
            skLineSegment(sketch, "E110", {"start": v(-40.71, -13) * mm, "end": v(-43.82, -15.95) * mm});
            skLineSegment(sketch, "E111", {"start": v(-43.82, -15.95) * mm, "end": v(-46.64, -13) * mm});
            skLineSegment(sketch, "E112", {"start": v(-46.64, -13) * mm, "end": v(-44.94, -13) * mm});
            skLineSegment(sketch, "E113", {"start": v(-44.94, -13) * mm, "end": v(-44.94, -3.2) * mm});
            skLineSegment(sketch, "E114.MirrorCS", {"start": v(-42.48, 6.6) * mm, "end": v(-40.71, 6.6) * mm});
            skLineSegment(sketch, "E115.MirrorCS", {"start": v(-46.64, 6.6) * mm, "end": v(-44.94, 6.6) * mm});
            skLineSegment(sketch, "E116.MirrorCS", {"start": v(-42.48, -3.2) * mm, "end": v(-42.48, 6.6) * mm});
            skLineSegment(sketch, "E117.MirrorCS", {"start": v(-43.82, 9.56) * mm, "end": v(-46.64, 6.6) * mm});
            skLineSegment(sketch, "E118.MirrorCS", {"start": v(-44.94, 6.6) * mm, "end": v(-44.94, -3.2) * mm});
            skLineSegment(sketch, "E119.MirrorCS", {"start": v(-40.71, 6.6) * mm, "end": v(-43.82, 9.56) * mm});
            skSolve(sketch);
        }
        {
            var Q0;
            Q0 = qSketchRegion(id + "F25", true);
            extrude(context, id + "F26", {"entities" : qUnion([Q0]), "operationType" : NewBodyOperationType.REMOVE, "oppositeDirection" : true, "depth" : 3 * mm});
        }
    });
